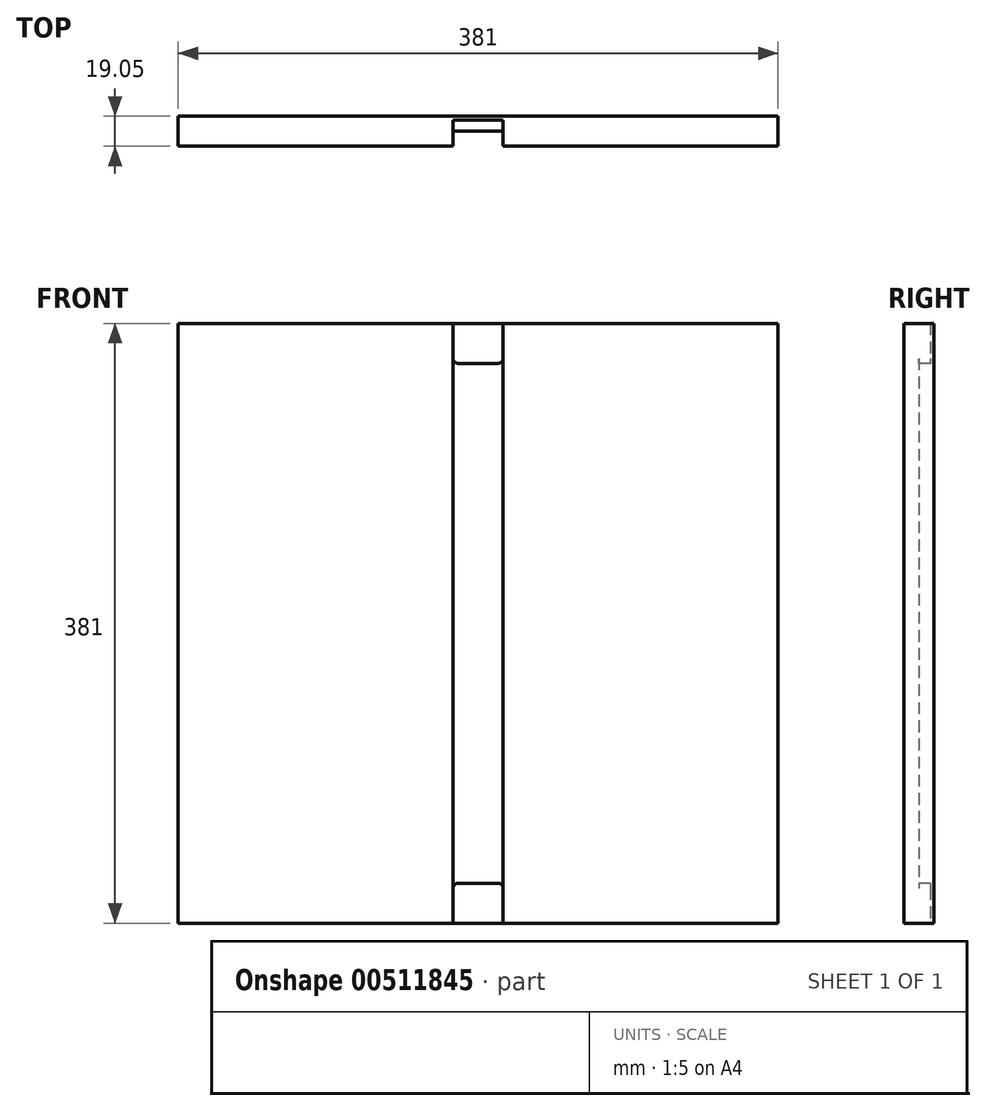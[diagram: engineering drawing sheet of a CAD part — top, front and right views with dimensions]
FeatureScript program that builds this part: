
annotation { "Feature Type Name" : "Feature", "Feature Type Description" : "" }
export const myFeature = defineFeature(function(context is Context, id is Id, definition is map)
    precondition{}
    {
        {
            var Q0;
            Q0=qCreatedBy(makeId("Front.planeOp"),FACE);
            var sketch = newSketch(context, id + "F0", { "sketchPlane" : qUnion([Q0])});
            skLineSegment(sketch, "E0.bottom", {"start": v(-198.81, 242.2) * mm, "end": v(182.19, 242.2) * mm});
            skLineSegment(sketch, "E0.top", {"start": v(-198.81, -138.8) * mm, "end": v(182.19, -138.8) * mm});
            skLineSegment(sketch, "E0.left", {"start": v(-198.81, 242.2) * mm, "end": v(-198.81, -138.8) * mm});
            skLineSegment(sketch, "E0.right", {"start": v(182.19, 242.2) * mm, "end": v(182.19, -138.8) * mm});
            skLineSegment(sketch, "E1", {"start": v(-8.31, 242.2) * mm, "end": v(-8.31, -138.8) * mm, "construction": true});
            skLineSegment(sketch, "E2.0", {"start": v(-24.19, 242.2) * mm, "end": v(-24.19, -138.8) * mm});
            skLineSegment(sketch, "E3.0", {"start": v(7.56, 242.2) * mm, "end": v(7.56, -138.8) * mm});
            skSolve(sketch);
        }
        {
            var Q0;
            {var subQ0=sQuery(id+"F0.wireOp",EDGE,"E0.left");Q0=makeQuery(id+"F0.imprint","IMPRINT",FACE,{"disambiguationData":[TD([[makeQuery(id+"F0.imprint","IMPRINT",EDGE,{"derivedFrom":subQ0}),1.0]])]});}
            var Q1;
            {var subQ0=sQuery(id+"F0.wireOp",EDGE,"E0.right");Q1=makeQuery(id+"F0.imprint","IMPRINT",FACE,{"disambiguationData":[TD([[makeQuery(id+"F0.imprint","IMPRINT",EDGE,{"derivedFrom":subQ0}),-1.0]])]});}
            extrude(context, id + "F1", {"entities" : qUnion([Q0, Q1]), "depth" : 12.7 * mm, "offsetDistance" : 25.4 * mm});
        }
        {
            var Q0;
            {var subQ0=sQuery(id+"F0.wireOp",EDGE,"E2.0");Q0=makeQuery(id+"F0.imprint","IMPRINT",FACE,{"disambiguationData":[TD([[makeQuery(id+"F0.imprint","IMPRINT",EDGE,{"derivedFrom":subQ0}),1.0]])]});}
            extrude(context, id + "F2", {"entities" : qUnion([Q0]), "operationType" : NewBodyOperationType.ADD, "depth" : 3.17 * mm, "offsetDistance" : 25.4 * mm});
        }
        {
            var Q0;
            Q0=makeQuery(id+"F1.opExtrude","CAP_FACE",FACE,{"disambiguationData":[OSD([sQuery(id+"F0.wireOp",EDGE,"E0.bottom"),sQuery(id+"F0.wireOp",EDGE,"E0.top"),sQuery(id+"F0.wireOp",EDGE,"E0.left"),sQuery(id+"F0.wireOp",EDGE,"E2.0")])],"isStart":false});
            var sketch = newSketch(context, id + "F3", { "sketchPlane" : qUnion([Q0])});
            skLineSegment(sketch, "E4.bottom", {"start": v(-24.19, -138.8) * mm, "end": v(7.56, -138.8) * mm});
            skLineSegment(sketch, "E4.top", {"start": v(-21.01, -113.4) * mm, "end": v(4.39, -113.4) * mm});
            skLineSegment(sketch, "E4.left", {"start": v(-24.19, -138.8) * mm, "end": v(-24.19, -116.57) * mm});
            skLineSegment(sketch, "E4.right", {"start": v(7.56, -138.8) * mm, "end": v(7.56, -116.57) * mm});
            skLineSegment(sketch, "E5", {"start": v(-24.19, 51.7) * mm, "end": v(14.66, 51.7) * mm, "construction": true});
            skPoint(sketch, "E5.endSnap0", {"position": v(-24.19, 51.7) * mm});
            skLineSegment(sketch, "E6.MirrorCS", {"start": v(-21.01, 216.8) * mm, "end": v(4.39, 216.8) * mm});
            skLineSegment(sketch, "E7.MirrorCS", {"start": v(-24.19, 242.2) * mm, "end": v(7.56, 242.2) * mm});
            skLineSegment(sketch, "E8.MirrorCS", {"start": v(-24.19, 242.2) * mm, "end": v(-24.19, 219.98) * mm});
            skLineSegment(sketch, "E9.MirrorCS", {"start": v(7.56, 242.2) * mm, "end": v(7.56, 219.98) * mm});
            skPoint(sketch, "E10.visualSharp", {"position": v(-24.19, -113.4) * mm});
            skArc(sketch, "E10.filletArc", {"start": v(-21.01, -113.4) * mm, "mid": v(-23.26, -114.32) * mm, "end": v(-24.19, -116.57) * mm});
            skPoint(sketch, "E11.visualSharp", {"position": v(7.56, -113.4) * mm});
            skArc(sketch, "E11.filletArc", {"start": v(7.56, -116.57) * mm, "mid": v(6.63, -114.32) * mm, "end": v(4.39, -113.4) * mm});
            skPoint(sketch, "E12.visualSharp", {"position": v(-24.19, 216.8) * mm});
            skArc(sketch, "E12.filletArc", {"start": v(-24.19, 219.98) * mm, "mid": v(-23.26, 217.74) * mm, "end": v(-21.01, 216.8) * mm});
            skPoint(sketch, "E13.visualSharp", {"position": v(7.56, 216.8) * mm});
            skArc(sketch, "E13.filletArc", {"start": v(4.39, 216.8) * mm, "mid": v(6.63, 217.74) * mm, "end": v(7.56, 219.98) * mm});
            skSolve(sketch);
        }
        {
            var Q0;
            {var subQ0=sQuery(id+"F0.wireOp",EDGE,"E0.right");Q0=makeQuery(id+"F0.imprint","IMPRINT",FACE,{"disambiguationData":[TD([[makeQuery(id+"F0.imprint","IMPRINT",EDGE,{"derivedFrom":subQ0}),-1.0]])]});}
            var sketch = newSketch(context, id + "F4", { "sketchPlane" : qUnion([Q0])});
            skLineSegment(sketch, "E14.0", {"start": v(-198.81, 242.2) * mm, "end": v(182.19, 242.2) * mm});
            skLineSegment(sketch, "E15.0", {"start": v(-198.81, -138.8) * mm, "end": v(182.19, -138.8) * mm});
            skLineSegment(sketch, "E16", {"start": v(182.19, 242.2) * mm, "end": v(182.19, -138.8) * mm});
            skLineSegment(sketch, "E17", {"start": v(-198.81, 242.2) * mm, "end": v(-198.81, -138.8) * mm});
            skSolve(sketch);
        }
        {
            var Q0;
            Q0 = qSketchRegion(id + "F4", true);
            extrude(context, id + "F5", {"entities" : qUnion([Q0]), "operationType" : NewBodyOperationType.ADD, "oppositeDirection" : true, "depth" : 6.35 * mm, "offsetDistance" : 25.4 * mm});
        }
        {
            var Q0;
            Q0=makeQuery(id+"F3.imprint","IMPRINT",FACE,{"disambiguationData":[TD([[makeQuery(id+"F3.imprint","IMPRINT",EDGE,{"derivedFrom":sQuery(id+"F3.wireOp",EDGE,"E4.bottom")}),1.0]])]});
            var Q1;
            Q1=makeQuery(id+"F3.imprint","IMPRINT",FACE,{"disambiguationData":[TD([[makeQuery(id+"F3.imprint","IMPRINT",EDGE,{"derivedFrom":sQuery(id+"F3.wireOp",EDGE,"E6.MirrorCS")}),1.0]])]});
            extrude(context, id + "F6", {"entities" : qUnion([Q0, Q1]), "operationType" : NewBodyOperationType.REMOVE, "oppositeDirection" : true, "depth" : 16.67 * mm, "offsetDistance" : 25.4 * mm});
        }
    });
